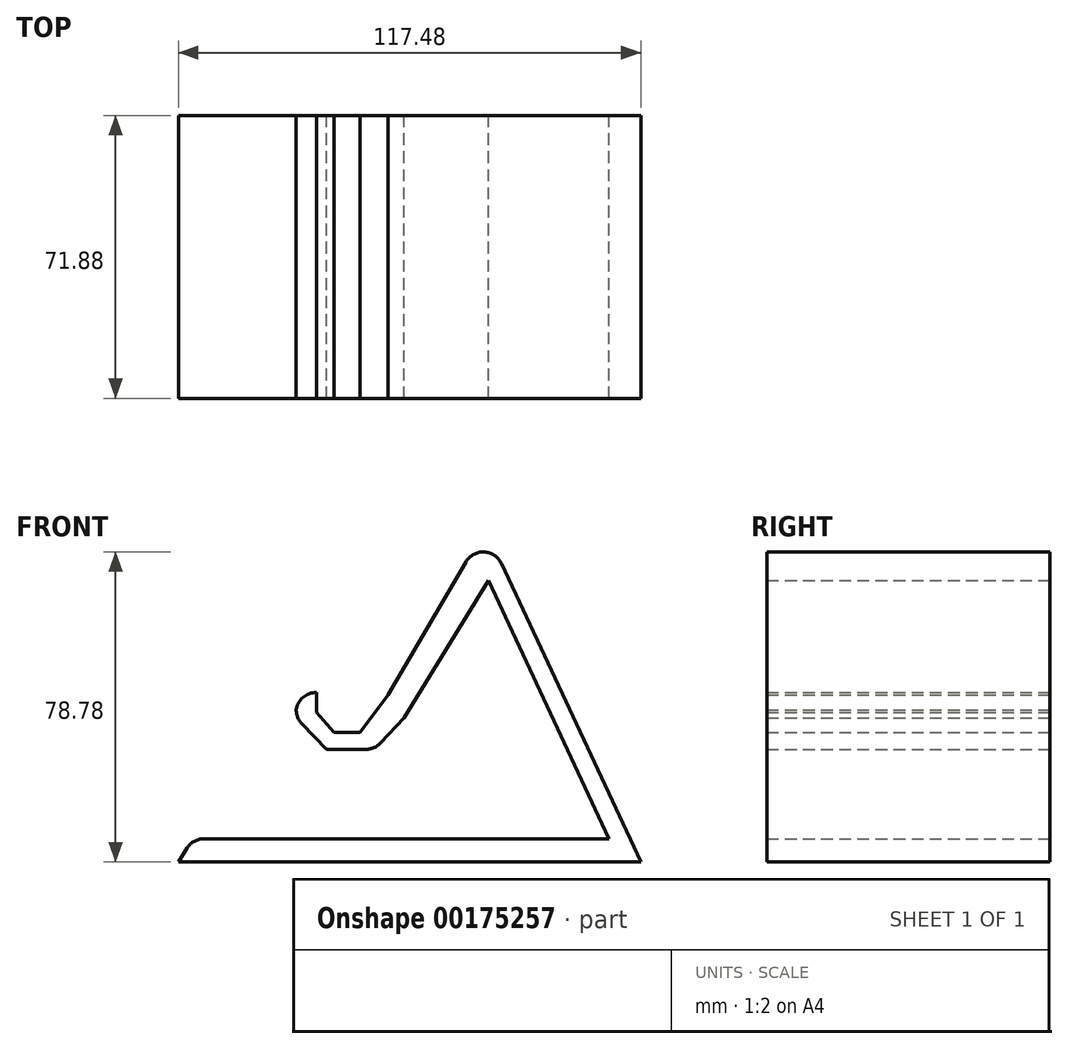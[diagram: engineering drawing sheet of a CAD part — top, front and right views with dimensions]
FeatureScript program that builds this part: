
annotation { "Feature Type Name" : "Feature", "Feature Type Description" : "" }
export const myFeature = defineFeature(function(context is Context, id is Id, definition is map)
    precondition{}
    {
        {
            var Q0;
            Q0=qCreatedBy(makeId("Front.planeOp"),FACE);
            var sketch = newSketch(context, id + "F0", { "sketchPlane" : qUnion([Q0])});
            skLineSegment(sketch, "E0", {"start": v(-35.83, 14.96) * mm, "end": v(-35.83, 9.42) * mm});
            skLineSegment(sketch, "E1", {"start": v(-35.83, 9.42) * mm, "end": v(-31.4, 4.25) * mm});
            skLineSegment(sketch, "E2", {"start": v(-31.4, 4.25) * mm, "end": v(-24.75, 4.25) * mm});
            skLineSegment(sketch, "E3", {"start": v(-24.75, 4.25) * mm, "end": v(-17.73, 13.85) * mm});
            skLineSegment(sketch, "E4", {"start": v(-17.73, 13.85) * mm, "end": v(7.02, 55.97) * mm});
            skLineSegment(sketch, "E5", {"start": v(7.02, 55.97) * mm, "end": v(46.55, -28.63) * mm});
            skLineSegment(sketch, "E6", {"start": v(46.55, -28.63) * mm, "end": v(-70.93, -28.63) * mm});
            skLineSegment(sketch, "E7", {"start": v(-70.93, -28.63) * mm, "end": v(-67.23, -22.72) * mm});
            skLineSegment(sketch, "E8", {"start": v(-67.23, -22.72) * mm, "end": v(38.42, -22.72) * mm});
            skLineSegment(sketch, "E9", {"start": v(38.42, -22.72) * mm, "end": v(7.78, 42.85) * mm});
            skLineSegment(sketch, "E10", {"start": v(7.78, 42.85) * mm, "end": v(-13.67, 7.94) * mm});
            skLineSegment(sketch, "E11", {"start": v(-13.67, 7.94) * mm, "end": v(-21.06, 0) * mm});
            skLineSegment(sketch, "E12", {"start": v(-21.06, 0) * mm, "end": v(-33.25, 0) * mm});
            skLineSegment(sketch, "E13", {"start": v(-33.25, 0) * mm, "end": v(-41, 7.94) * mm});
            skLineSegment(sketch, "E14", {"start": v(-41, 7.94) * mm, "end": v(-41, 17.55) * mm});
            skLineSegment(sketch, "E15", {"start": v(-41, 17.55) * mm, "end": v(-35.83, 14.96) * mm});
            skSolve(sketch);
        }
        {
            var Q0;
            Q0=qSketchRegion(id+"F0",true);
            extrude(context, id + "F1", {"entities" : qUnion([Q0]), "depth" : 71.88 * mm});
        }
        {
            var Q0;
            Q0=makeQuery(id+"F1.opExtrude","SWEPT_EDGE",EDGE,{"disambiguationData":[OSD([sQuery(id+"F0.wireOp",EDGE,"E13"),sQuery(id+"F0.wireOp",EDGE,"E14")])]});
            fillet(context, id + "F2", {"entities" : qUnion([Q0]), "radius" : 5.08 * mm, "tangentPropagation" : true, "allowEdgeOverflow" : false});
        }
        {
            var Q0;
            Q0=makeQuery(id+"F1.opExtrude","SWEPT_EDGE",EDGE,{"disambiguationData":[OSD([sQuery(id+"F0.wireOp",EDGE,"E14"),sQuery(id+"F0.wireOp",EDGE,"E15")])]});
            var Q1;
            Q1=makeQuery(id+"F1.opExtrude","SWEPT_EDGE",EDGE,{"disambiguationData":[OSD([sQuery(id+"F0.wireOp",EDGE,"E7"),sQuery(id+"F0.wireOp",EDGE,"E8")])]});
            var Q2;
            Q2=makeQuery(id+"F1.opExtrude","SWEPT_EDGE",EDGE,{"disambiguationData":[OSD([sQuery(id+"F0.wireOp",EDGE,"E4"),sQuery(id+"F0.wireOp",EDGE,"E5")])]});
            var Q3;
            Q3=makeQuery(id+"F1.opExtrude","SWEPT_EDGE",EDGE,{"disambiguationData":[OSD([sQuery(id+"F0.wireOp",EDGE,"E11"),sQuery(id+"F0.wireOp",EDGE,"E12")])]});
            fillet(context, id + "F3", {"entities" : qUnion([Q0, Q1, Q2, Q3]), "radius" : 5.08 * mm, "tangentPropagation" : true, "allowEdgeOverflow" : false});
        }
    });
